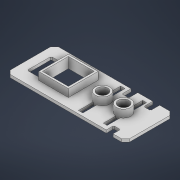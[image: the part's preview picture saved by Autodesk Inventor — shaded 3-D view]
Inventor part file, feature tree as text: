
AUTODESK INVENTOR PART (.ipt)
format: ipt  version: 2021 (Build 250183000, 183)  size: 285,184 bytes
history: native  units: mm
features: sketch x10, extrude x8, chamfer x3, hole x1, emboss x1
ambient origin geometry x8: Origin, YZ Plane, XZ Plane, XY Plane, X Axis, Y Axis, Z Axis, Center Point
bodies: Solid1 (feature_tree)
feature tree (23):
  extrude  "Extrusion1"  Depth=25.0mm
  hole  "Hole1"  [1 undecoded]
  extrude  "Extrusion2"  Depth=1.0mm
  emboss  "Emboss1"
  extrude  "Extrusion3"  Depth=4.0mm TaperAngle=0.0deg
  extrude  "Extrusion4"  Depth=0.5mm TaperAngle=0.0deg
  extrude  "Extrusion5"  Depth=13.5mm
  extrude  "Extrusion6"  Depth=1.0mm
  extrude  "Extrusion7"  Depth=0.75mm
  extrude  "Extrusion8"  TaperAngle=0.0deg  [1 undecoded]
  chamfer  "Chamfer1"  Distance=4.5mm
  chamfer  "Chamfer2"  Distance=3.5mm
  chamfer  "Chamfer3"  [1 undecoded]
  sketch  "Sketch1"  dims[d0=62.0mm d1=25.0mm]
  sketch  "Sketch2"  dims[d2=1.5mm d3=0.0mm d4=11.0mm]
  sketch  "Sketch3"  dims[d5=13.5mm]
  sketch  "Sketch4"  dims[d6=5.5mm d7=6.0mm d8=4.0mm d9=2.0mm d10=90.0deg d11=8.0mm d12=20.594885mm d13=1.0mm]
  sketch  "Sketch5"  dims[d14=1.0mm d15=4.0mm d16=0.0mm]
  sketch  "Sketch6"  dims[d17=6.2mm d18=0.5mm d19=0.0mm]
  sketch  "Sketch7"  dims[d20=11.0mm d21=13.5mm]
  sketch  "Sketch8"  dims[d22=0.0mm d23=0.0mm d24=1.0mm]
  sketch  "Sketch9"  dims[d25=1.5mm d26=0.0mm d28=0.75mm]
  sketch  "Sketch10"  dims[d30=3.25mm d31=0.0mm d32=0.0mm d33=4.5mm d34=3.5mm d36=0.0mm d37=0.0mm d38=1.5mm d39=0.0mm d40=7.0mm d41=4.5mm d42=0.0mm d43=0.0mm d44=0.5mm d45=2.0mm d46=45.0deg d47=0.1mm d48=2.0mm d49=45.0deg d50=2.0mm d51=2.0mm d52=45.0deg d53=0.75mm d54=3.5mm d55=3.8mm d57=3.8mm d58=12.5mm d60=4.5mm d61=0.7mm d62=20.5mm d63=2.0mm d64=1.5mm]
note: 3 required parameter values undecoded (feature->parameter linkage not recoverable at this tier; creation-order binding heuristic only, values carry confidence <= 0.55)
